# Revit family: E511.01.03_D6
name_source: partatom
category: Plumbing Fixtures
units: mm (PartAtom-declared; Revit-internal decimal feet)

## family parameters
Always vertical = Yes
Cut with Voids When Loaded = No
Enable Cutting in Views = Yes
Maintain Annotation Orientation = No
OmniClass Number = 23.45.55.17
OmniClass Title = Mixing Faucets
Part Type = Normal
Room Calculation Point = No
Round Connector Dimension = Use Diameter
Shared = No
Work Plane-Based = No

## types (1)
- Standard
    Acabado = Cromo
    CW Connection = Yes
    Catalog web link = https://fvandina.com
    Certificación = INEN
    Conexión hidráulica = W9/16" x 19
    Connector_1_Diameter = 0' - 0 13/32"
    Connector_2_Diameter = 0' - 0 13/32"
    Cota alto = 138 mm
    Cota ancho = 50 mm
    Cota largo = 106 mm
    Default Elevation = 0' - 0"
    Description = Juego Mezclador Monocomando para Picos Colorflex ELIPSIS
    Dirección fabricante = KM 25, VÍA SANGOLQUÍ AMAGUAÑA - PICHINCHA - ECUADOR
    Garantía = GARANTÍA TOTAL FV - DETALLES EN PÁGINA WEB
    HW Connection = Yes
    Instalación = https://fvandina.com
    Manufacturer = FV – ÁREA ANDINA S.A.
    Material = Latón
    Model = E511.01.03/D6
    Part Number = E511.01.03/D6
    Presión = 60 PSI
    Title = Juego Mezclador Monocomando para Picos Colorflex ELIPSIS
    URL = www.fvandina.com
    Vent Connection = No
    Waste Connection = No

## geometry (parser evidence)
native form markers: Sweep x3
no freeform markers — native parametric forms only
